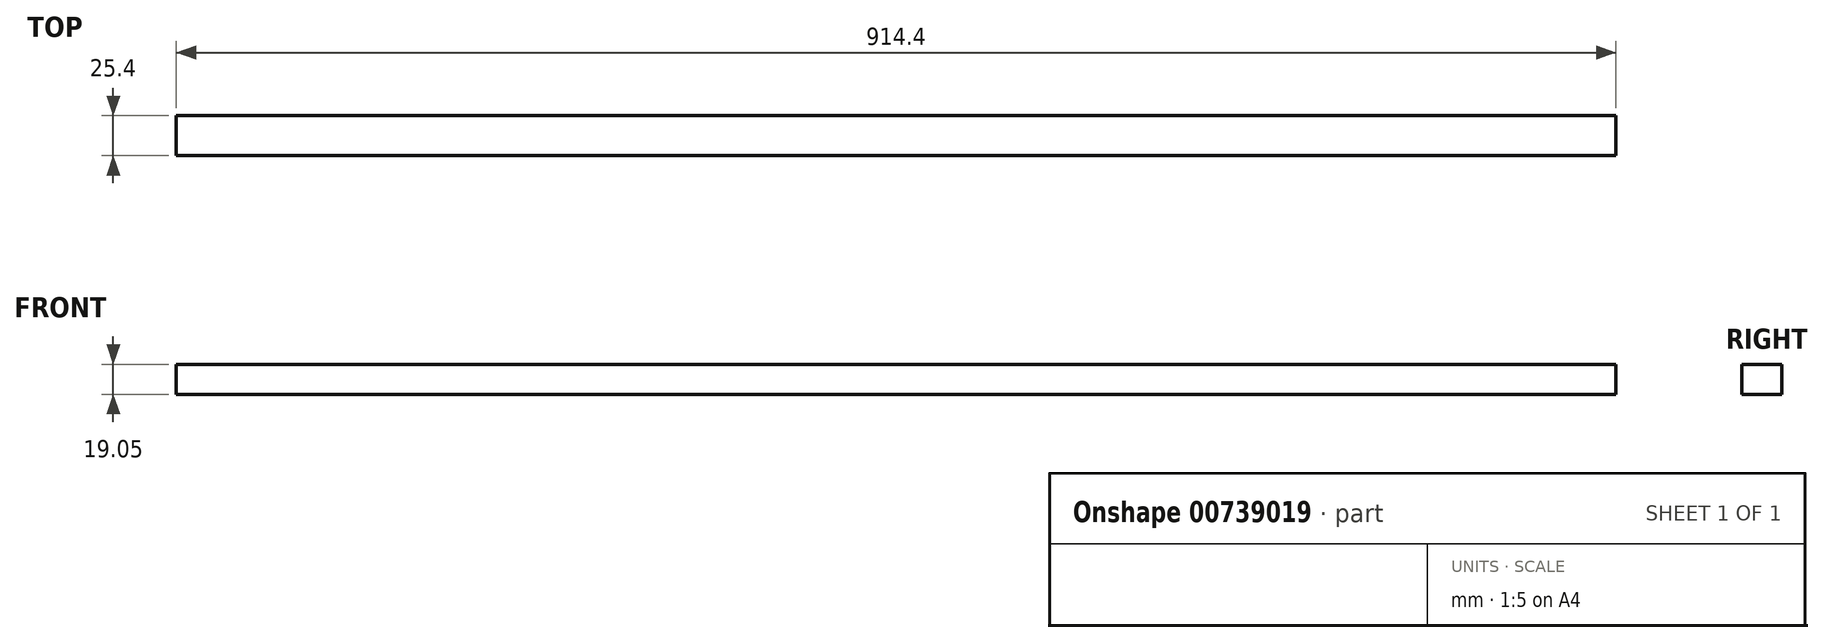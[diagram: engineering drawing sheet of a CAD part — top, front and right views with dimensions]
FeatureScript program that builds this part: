
annotation { "Feature Type Name" : "Feature", "Feature Type Description" : "" }
export const myFeature = defineFeature(function(context is Context, id is Id, definition is map)
    precondition{}
    {
        {
            var Q0;
            Q0=qCreatedBy(makeId("Top.planeOp"),FACE);
            var sketch = newSketch(context, id + "F0", { "sketchPlane" : qUnion([Q0])});
            skLineSegment(sketch, "E0.bottom", {"start": v(-47.89, 75.42) * mm, "end": v(866.51, 75.42) * mm});
            skLineSegment(sketch, "E0.top", {"start": v(-47.89, 50.02) * mm, "end": v(866.51, 50.02) * mm});
            skLineSegment(sketch, "E0.left", {"start": v(-47.89, 75.42) * mm, "end": v(-47.89, 50.02) * mm});
            skLineSegment(sketch, "E0.right", {"start": v(866.51, 75.42) * mm, "end": v(866.51, 50.02) * mm});
            skSolve(sketch);
        }
        {
            var Q0;
            Q0=makeQuery(id+"F0.imprint","IMPRINT",FACE,{"disambiguationData":[TD([[makeQuery(id+"F0.imprint","IMPRINT",EDGE,{"derivedFrom":sQuery(id+"F0.wireOp",EDGE,"E0.bottom")}),-1.0]])]});
            extrude(context, id + "F1", {"entities" : qUnion([Q0]), "oppositeDirection" : true, "depth" : 19.05 * mm, "offsetDistance" : 25.4 * mm});
        }
    });
